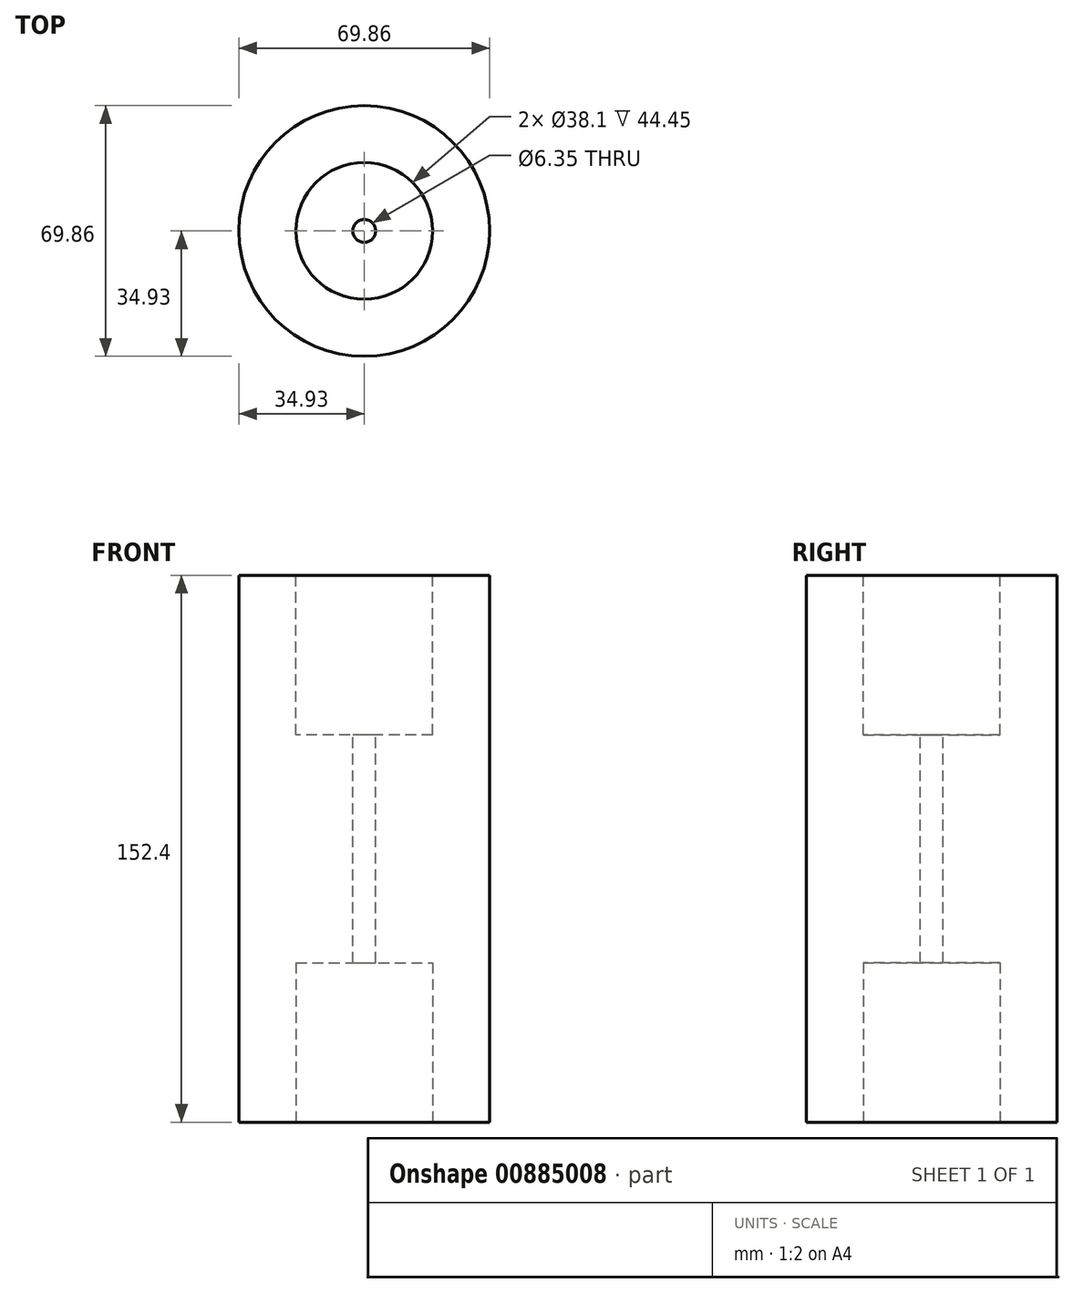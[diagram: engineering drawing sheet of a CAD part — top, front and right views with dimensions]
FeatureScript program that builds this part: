
annotation { "Feature Type Name" : "Feature", "Feature Type Description" : "" }
export const myFeature = defineFeature(function(context is Context, id is Id, definition is map)
    precondition{}
    {
        {
            var Q0;
            Q0=qCreatedBy(makeId("Top.planeOp"),FACE);
            var sketch = newSketch(context, id + "F0", { "sketchPlane" : qUnion([Q0])});
            skCircle(sketch, "E0", {"center": v(0, 0) * mm, "radius": 34.93 * mm});
            skSolve(sketch);
        }
        {
            var Q0;
            Q0=makeQuery(id+"F0.imprint","IMPRINT",FACE,{"disambiguationData":[TD([[makeQuery(id+"F0.imprint","IMPRINT",EDGE,{"derivedFrom":sQuery(id+"F0.wireOp",EDGE,"E0")}),1.0]])]});
            extrude(context, id + "F1", {"entities" : qUnion([Q0]), "depth" : 152.4 * mm, "offsetDistance" : 25.4 * mm});
        }
        {
            var Q0;
            Q0=makeQuery(id+"F1.opExtrude","CAP_FACE",FACE,{"disambiguationData":[OSD([sQuery(id+"F0.wireOp",EDGE,"E0")])],"isStart":true});
            var sketch = newSketch(context, id + "F2", { "sketchPlane" : qUnion([Q0])});
            skCircle(sketch, "E1", {"center": v(0, 0) * mm, "radius": 19.05 * mm});
            skSolve(sketch);
        }
        {
            var Q0;
            Q0=makeQuery(id+"F2.imprint","IMPRINT",FACE,{"disambiguationData":[TD([[makeQuery(id+"F2.imprint","IMPRINT",EDGE,{"derivedFrom":sQuery(id+"F2.wireOp",EDGE,"E1")}),1.0]])]});
            extrude(context, id + "F3", {"entities" : qUnion([Q0]), "operationType" : NewBodyOperationType.REMOVE, "oppositeDirection" : true, "depth" : 44.45 * mm, "offsetDistance" : 25.4 * mm});
        }
        {
            var Q0;
            Q0=makeQuery(id+"F1.opExtrude","CAP_FACE",FACE,{"disambiguationData":[OSD([sQuery(id+"F0.wireOp",EDGE,"E0")])],"isStart":false});
            var sketch = newSketch(context, id + "F4", { "sketchPlane" : qUnion([Q0])});
            skCircle(sketch, "E2", {"center": v(0, 0) * mm, "radius": 19.05 * mm});
            skSolve(sketch);
        }
        {
            var Q0;
            Q0=makeQuery(id+"F4.imprint","IMPRINT",FACE,{"disambiguationData":[TD([[makeQuery(id+"F4.imprint","IMPRINT",EDGE,{"derivedFrom":sQuery(id+"F4.wireOp",EDGE,"E2")}),1.0]])]});
            extrude(context, id + "F5", {"entities" : qUnion([Q0]), "operationType" : NewBodyOperationType.REMOVE, "oppositeDirection" : true, "depth" : 44.45 * mm, "offsetDistance" : 25.4 * mm});
        }
        {
            var Q0;
            Q0=makeQuery(id+"F5.boolean.opBoolean","COPY",FACE,{"derivedFrom":makeQuery(id+"F5.opExtrude","CAP_FACE",FACE,{"disambiguationData":[OSD([sQuery(id+"F4.wireOp",EDGE,"E2")])],"isStart":false})});
            var sketch = newSketch(context, id + "F6", { "sketchPlane" : qUnion([Q0])});
            skCircle(sketch, "E3", {"center": v(0, 0) * mm, "radius": 3.18 * mm});
            skSolve(sketch);
        }
        {
            var Q0;
            Q0=makeQuery(id+"F6.imprint","IMPRINT",FACE,{"disambiguationData":[TD([[makeQuery(id+"F6.imprint","IMPRINT",EDGE,{"derivedFrom":sQuery(id+"F6.wireOp",EDGE,"E3")}),1.0]])]});
            var Q1;
            Q1=sQuery(id+"F6.wireOp",EDGE,"E3");
            extrude(context, id + "F7", {"entities" : qUnion([Q0]), "operationType" : NewBodyOperationType.REMOVE, "surfaceEntities" : qUnion([Q1]), "oppositeDirection" : true, "depth" : 152.4 * mm, "offsetDistance" : 25.4 * mm});
        }
    });
